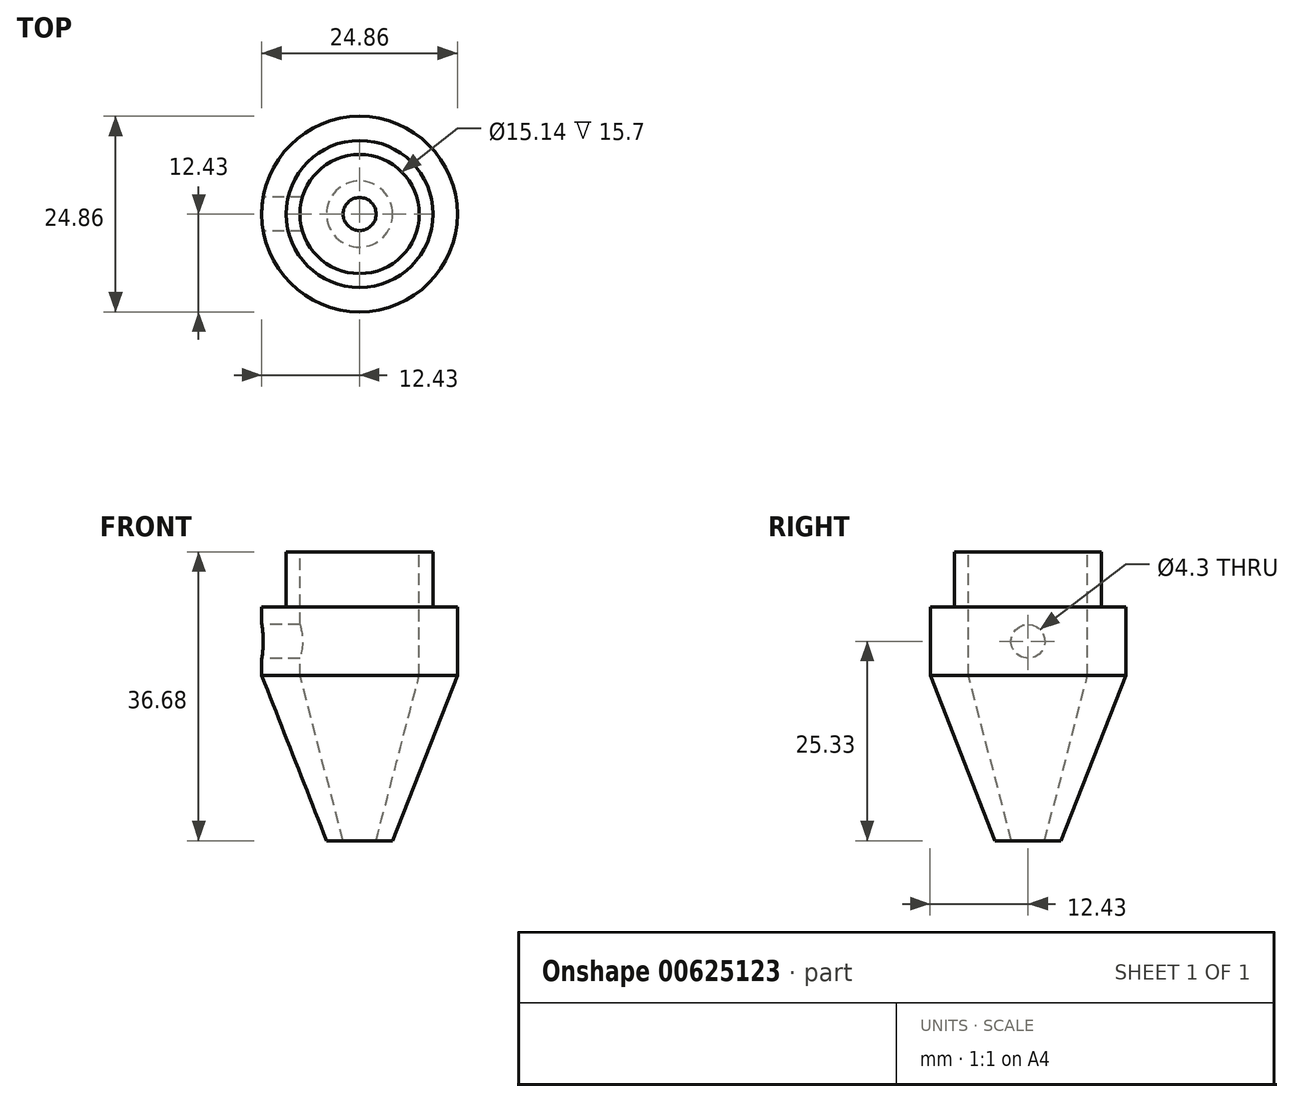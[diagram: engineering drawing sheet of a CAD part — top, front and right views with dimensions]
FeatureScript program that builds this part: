
annotation { "Feature Type Name" : "Feature", "Feature Type Description" : "" }
export const myFeature = defineFeature(function(context is Context, id is Id, definition is map)
    precondition{}
    {
        {
            var Q0;
            Q0=qCreatedBy(makeId("Top.planeOp"),FACE);
            var sketch = newSketch(context, id + "F0", { "sketchPlane" : qUnion([Q0])});
            skCircle(sketch, "E0", {"center": v(0, 0) * mm, "radius": 9.34 * mm});
            skSolve(sketch);
        }
        {
            var Q0;
            Q0=makeQuery(id+"F0.imprint","IMPRINT",FACE,{"disambiguationData":[TD([[makeQuery(id+"F0.imprint","IMPRINT",EDGE,{"derivedFrom":sQuery(id+"F0.wireOp",EDGE,"E0")}),1.0]])]});
            extrude(context, id + "F1", {"entities" : qUnion([Q0]), "oppositeDirection" : true, "depth" : 7 * mm, "offsetDistance" : 25 * mm});
        }
        {
            var Q0;
            Q0=makeQuery(id+"F1.opExtrude","CAP_FACE",FACE,{"disambiguationData":[OSD([sQuery(id+"F0.wireOp",EDGE,"E0")])],"isStart":false});
            var sketch = newSketch(context, id + "F2", { "sketchPlane" : qUnion([Q0])});
            skCircle(sketch, "E1", {"center": v(0, 0) * mm, "radius": 12.43 * mm});
            skSolve(sketch);
        }
        {
            var Q0;
            Q0=makeQuery(id+"F2.imprint","IMPRINT",FACE,{"disambiguationData":[TD([[makeQuery(id+"F2.imprint","IMPRINT",EDGE,{"derivedFrom":sQuery(id+"F2.wireOp",EDGE,"E1")}),1.0]])]});
            var Q1;
            Q1=makeQuery(id+"F2.imprint","IMPRINT",FACE,{"disambiguationData":[TD([[makeQuery(id+"F2.imprint","IMPRINT",EDGE,{"derivedFrom":makeQuery(id+"F1.opExtrude","CAP_EDGE",EDGE,{"disambiguationData":[OSD([sQuery(id+"F0.wireOp",EDGE,"E0")])],"isStart":false})}),-1.0]])]});
            extrude(context, id + "F3", {"entities" : qUnion([Q0, Q1]), "operationType" : NewBodyOperationType.ADD, "depth" : 8.7 * mm, "offsetDistance" : 25 * mm});
        }
        {
            var Q0;
            Q0=makeQuery(id+"F3.opExtrude","CAP_FACE",FACE,{"disambiguationData":[OSD([sQuery(id+"F2.wireOp",EDGE,"E1")])],"isStart":false});
            cPlane(context, id + "F4", {"entities" : qUnion([Q0]), "cplaneType" : CPlaneType.OFFSET, "offset" : 20.98 * mm, "width" : 150 * mm, "height" : 150 * mm});
        }
        {
            var Q0;
            Q0=qCreatedBy(id+"F4.planeOp",FACE);
            var sketch = newSketch(context, id + "F5", { "sketchPlane" : qUnion([Q0])});
            skCircle(sketch, "E2", {"center": v(0, 0) * mm, "radius": 4.2 * mm});
            skSolve(sketch);
        }
        {
            var Q1;
            Q1=makeQuery(id+"F3.opExtrude","CAP_FACE",FACE,{"disambiguationData":[OSD([sQuery(id+"F2.wireOp",EDGE,"E1")])],"isStart":false});
            var Q2;
            Q2=makeQuery(id+"F5.imprint","IMPRINT",FACE,{"disambiguationData":[TD([[makeQuery(id+"F5.imprint","IMPRINT",EDGE,{"derivedFrom":sQuery(id+"F5.wireOp",EDGE,"E2")}),1.0]])]});
            loft(context, id + "F6", {"operationType" : NewBodyOperationType.ADD, "sheetProfilesArray" : [{ "sheetProfileEntities" : qUnion([Q1]) }, { "sheetProfileEntities" : qUnion([Q2]) }]});
        }
        {
            var Q0;
            Q0=qCreatedBy(makeId("Right.planeOp"),FACE);
            cPlane(context, id + "F7", {"entities" : qUnion([Q0]), "cplaneType" : CPlaneType.OFFSET, "offset" : 12.43 * mm, "oppositeDirection" : true, "width" : 150 * mm, "height" : 150 * mm});
        }
        {
            var Q0;
            Q0=makeQuery(id+"F1.opExtrude","CAP_FACE",FACE,{"disambiguationData":[OSD([sQuery(id+"F0.wireOp",EDGE,"E0")])],"isStart":true});
            var sketch = newSketch(context, id + "F8", { "sketchPlane" : qUnion([Q0])});
            skCircle(sketch, "E3", {"center": v(0, 0) * mm, "radius": 7.57 * mm});
            skSolve(sketch);
        }
        {
            var Q0;
            Q0=makeQuery(id+"F6.opLoft","CAP_FACE",FACE,{"disambiguationData":[OSD([makeQuery(id+"F5.imprint","IMPRINT",FACE,{"disambiguationData":[TD([[makeQuery(id+"F5.imprint","IMPRINT",EDGE,{"derivedFrom":sQuery(id+"F5.wireOp",EDGE,"E2")}),1.0]])]})])],"isStart":true});
            var sketch = newSketch(context, id + "F9", { "sketchPlane" : qUnion([Q0])});
            skCircle(sketch, "E4", {"center": v(0, 0) * mm, "radius": 2.1 * mm});
            skSolve(sketch);
        }
        {
            var Q0;
            Q0=makeQuery(id+"F8.imprint","IMPRINT",FACE,{"disambiguationData":[TD([[makeQuery(id+"F8.imprint","IMPRINT",EDGE,{"derivedFrom":sQuery(id+"F8.wireOp",EDGE,"E3")}),1.0]])]});
            var Q1;
            Q1=sQuery(id+"F8.wireOp",EDGE,"E3");
            extrude(context, id + "F10", {"entities" : qUnion([Q0]), "operationType" : NewBodyOperationType.REMOVE, "surfaceEntities" : qUnion([Q1]), "oppositeDirection" : true, "depth" : 15.7 * mm, "offsetDistance" : 25 * mm});
        }
        {
            var Q0;
            Q0=makeQuery(id+"F10.boolean.opBoolean","COPY",FACE,{"derivedFrom":makeQuery(id+"F10.opExtrude","CAP_FACE",FACE,{"disambiguationData":[OSD([sQuery(id+"F8.wireOp",EDGE,"E3")])],"isStart":false})});
            var sketch = newSketch(context, id + "F11", { "sketchPlane" : qUnion([Q0])});
            skCircle(sketch, "E5.0", {"center": v(0, 0) * mm, "radius": 7.57 * mm});
            skSolve(sketch);
        }
        {
            var Q1;
            Q1=makeQuery(id+"F11.imprint","IMPRINT",FACE,{"disambiguationData":[TD([[makeQuery(id+"F11.imprint","IMPRINT",EDGE,{"derivedFrom":sQuery(id+"F11.wireOp",EDGE,"E5.0")}),1.0]])]});
            var Q2;
            Q2=makeQuery(id+"F9.imprint","IMPRINT",FACE,{"disambiguationData":[TD([[makeQuery(id+"F9.imprint","IMPRINT",EDGE,{"derivedFrom":sQuery(id+"F9.wireOp",EDGE,"E4")}),1.0]])]});
            loft(context, id + "F12", {"operationType" : NewBodyOperationType.REMOVE, "sheetProfilesArray" : [{ "sheetProfileEntities" : qUnion([Q1]) }, { "sheetProfileEntities" : qUnion([Q2]) }]});
        }
        {
            var Q0;
            Q0=qCreatedBy(id+"F7.planeOp",FACE);
            var sketch = newSketch(context, id + "F13", { "sketchPlane" : qUnion([Q0])});
            skLineSegment(sketch, "E6.0", {"start": v(12.43, -7) * mm, "end": v(-12.43, -7) * mm, "construction": true});
            skLineSegment(sketch, "E7.0", {"start": v(12.43, -15.7) * mm, "end": v(-12.43, -15.7) * mm, "construction": true});
            skLineSegment(sketch, "E8", {"start": v(0, -7) * mm, "end": v(0, -15.7) * mm, "construction": true});
            skCircle(sketch, "E9", {"center": v(0, -11.35) * mm, "radius": 2.15 * mm});
            skSolve(sketch);
        }
        {
            var Q0;
            Q0=makeQuery(id+"F13.imprint","IMPRINT",FACE,{"disambiguationData":[TD([[makeQuery(id+"F13.imprint","IMPRINT",EDGE,{"derivedFrom":sQuery(id+"F13.wireOp",EDGE,"E9")}),1.0]])]});
            var Q1;
            Q1=makeQuery(id+"F10.boolean.opBoolean","COPY",FACE,{"derivedFrom":makeQuery(id+"F10.opExtrude","SWEPT_FACE",FACE,{"disambiguationData":[OSD([sQuery(id+"F8.wireOp",EDGE,"E3")])]})});
            extrude(context, id + "F14", {"entities" : qUnion([Q0]), "operationType" : NewBodyOperationType.REMOVE, "endBound" : BoundingType.UP_TO_SURFACE, "depth" : 25 * mm, "endBoundEntityFace" : qUnion([Q1]), "offsetDistance" : 25 * mm});
        }
    });
